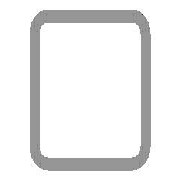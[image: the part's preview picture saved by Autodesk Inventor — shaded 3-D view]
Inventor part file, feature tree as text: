
AUTODESK INVENTOR PART (.ipt)
format: ipt  version: 2025.3 (Build 293356030, 356C)  size: 150,528 bytes
history: native  units: mm (DEFAULTED — no unit token found)
features: other x4, plane x3, split x2, sketch x1
ambient origin geometry x8: Origin, YZ Plane, XZ Plane, XY Plane, X Axis, Y Axis, Z Axis, Center Point
bodies: Solid1 (feature_tree), Body (feature_tree)
feature tree (10):
  parser-record x1  (decoder bookkeeping rows leaked as tree rows — omitted from the tree; the rows remain in map.json)
  other  "Driven Length"
  other  "Start plane"
  other  "End plane"
  plane  "Work Plane4"
  split  "Split1"
  plane  "Work Plane5"
  split  "Split2"
  sketch  "Sketch3"  dims[d3=707.106781mm d4=0.0mm d7=6.0mm d9=60.0mm d11=60.0mm d12=3.0mm d13=141.421356mm d14=848.528137mm d15=30.0mm d16=30.0mm d17=90.0deg d18=707.106781mm]
  plane  "Work Plane3"
